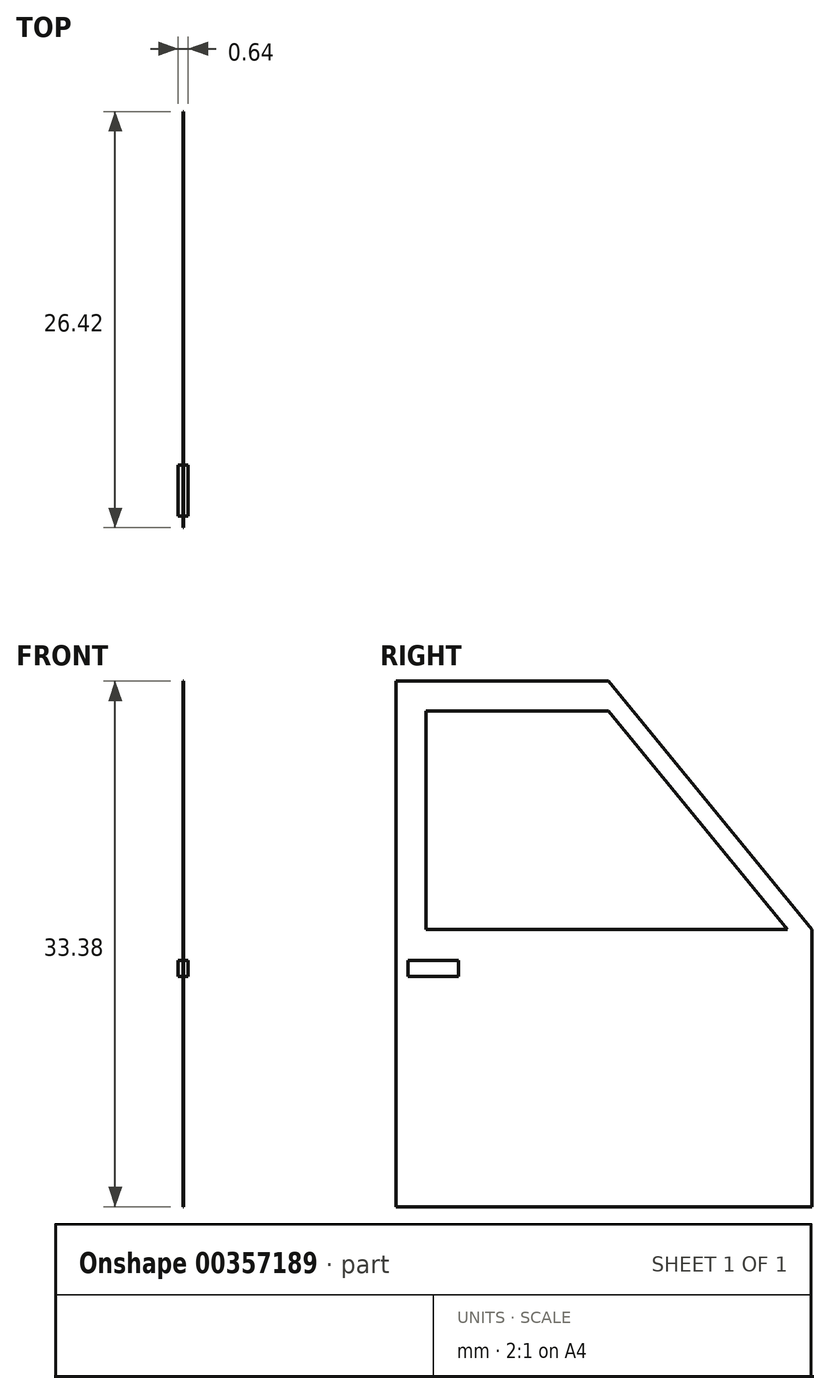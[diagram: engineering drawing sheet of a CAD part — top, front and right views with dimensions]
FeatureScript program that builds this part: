
annotation { "Feature Type Name" : "Feature", "Feature Type Description" : "" }
export const myFeature = defineFeature(function(context is Context, id is Id, definition is map)
    precondition{}
    {
        {
            var Q0;
            Q0=qCreatedBy(makeId("Right.planeOp"),FACE);
            var sketch = newSketch(context, id + "F0", { "sketchPlane" : qUnion([Q0])});
            skLineSegment(sketch, "E0", {"start": v(0, 19.89) * mm, "end": v(0, -13.49) * mm});
            skLineSegment(sketch, "E1", {"start": v(0, 19.89) * mm, "end": v(13.49, 19.89) * mm});
            skLineSegment(sketch, "E2", {"start": v(0, -13.49) * mm, "end": v(26.42, -13.49) * mm});
            skLineSegment(sketch, "E3", {"start": v(26.42, -13.49) * mm, "end": v(26.42, 4.11) * mm});
            skLineSegment(sketch, "E4", {"start": v(13.49, 19.89) * mm, "end": v(26.42, 4.11) * mm});
            skLineSegment(sketch, "E5", {"start": v(1.91, 4.11) * mm, "end": v(24.86, 4.11) * mm});
            skLineSegment(sketch, "E6", {"start": v(24.86, 4.11) * mm, "end": v(13.49, 18) * mm});
            skLineSegment(sketch, "E7", {"start": v(13.49, 18) * mm, "end": v(1.91, 18) * mm});
            skLineSegment(sketch, "E8", {"start": v(1.91, 18) * mm, "end": v(1.91, 4.11) * mm});
            skLineSegment(sketch, "E9", {"start": v(1.91, 2.14) * mm, "end": v(3.98, 2.14) * mm});
            skLineSegment(sketch, "E10", {"start": v(3.98, 2.14) * mm, "end": v(3.98, 1.15) * mm});
            skLineSegment(sketch, "E11", {"start": v(3.98, 1.15) * mm, "end": v(0.75, 1.15) * mm});
            skLineSegment(sketch, "E12", {"start": v(0.75, 1.15) * mm, "end": v(0.75, 2.14) * mm});
            skLineSegment(sketch, "E13", {"start": v(0.75, 2.14) * mm, "end": v(1.91, 2.14) * mm});
            skSolve(sketch);
        }
        {
            var Q0;
            Q0=makeQuery(id+"F0.imprint","IMPRINT",FACE,{"disambiguationData":[TD([[makeQuery(id+"F0.imprint","IMPRINT",EDGE,{"derivedFrom":sQuery(id+"F0.wireOp",EDGE,"E9")}),-1.0]])]});
            extrude(context, id + "F1", {"entities" : qUnion([Q0]), "endBound" : BoundingType.SYMMETRIC, "depth" : 0.64 * mm});
        }
        {
            var Q0;
            Q0=makeQuery(id+"F0.imprint","IMPRINT",FACE,{"disambiguationData":[TD([[makeQuery(id+"F0.imprint","IMPRINT",EDGE,{"derivedFrom":sQuery(id+"F0.wireOp",EDGE,"E0")}),1.0]])]});
            extrude(context, id + "F2", {"entities" : qUnion([Q0]), "operationType" : NewBodyOperationType.ADD, "depth" : 0.03 * mm});
        }
    });
